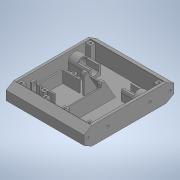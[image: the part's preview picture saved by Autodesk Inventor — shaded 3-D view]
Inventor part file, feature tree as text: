
AUTODESK INVENTOR PART (.ipt)
format: ipt  version: 2020 (Build 240168000, 168)  size: 648,192 bytes
history: native  units: in
note: dims shown in document units (in); Inventor stores cm internally (conversion verified against a paired STEP export)
features: extrude x19, sketch x19, projected_geometry x14, mirror x6, plane x1
ambient origin geometry x8: Origin, YZ Plane, XZ Plane, XY Plane, X Axis, Y Axis, Z Axis, Center Point
bodies: Solid1 (feature_tree)
feature tree (59):
  extrude  "Extrusion1"  Depth=5.9055in
  extrude  "Extrusion2"  TaperAngle=0.0deg  [1 undecoded]
  extrude  "Extrusion3"  Depth=1.063in
  extrude  "Extrusion4"  Depth=0.315in
  extrude  "Extrusion5"  TaperAngle=0.0deg  [1 undecoded]
  extrude  "Extrusion6"  Depth=0.5906in
  mirror  "Mirror1"
  extrude  "Extrusion7"  Depth=0.0787in
  mirror  "Mirror2"
  extrude  "Extrusion8"  Depth=0.6102in
  mirror  "Mirror3"
  plane  "Work Plane1"
  extrude  "Extrusion9"  Depth=0.7874in TaperAngle=0.0deg
  mirror  "Mirror4"
  extrude  "Extrusion10"  Depth=6.063in TaperAngle=0.0deg
  extrude  "Extrusion11"  Depth=0.1575in
  extrude  "Extrusion12"  TaperAngle=0.0deg  [1 undecoded]
  extrude  "Extrusion13"  Depth=0.2756in
  extrude  "Extrusion14"  Depth=0.4331in
  extrude  "Extrusion17"  Depth=2.7559in
  extrude  "Extrusion18"  Depth=0.0453in
  mirror  "Mirror6"
  extrude  "Extrusion19"  TaperAngle=0.0deg  [1 undecoded]
  mirror  "Mirror7"
  extrude  "Extrusion20"  Depth=0.0787in
  extrude  "Extrusion21"  Depth=0.993in
  sketch  "Sketch1"  dims[d0=1.1811in d1=5.9055in]
  sketch  "Sketch2"  dims[d2=5.1181in d3=0.0in]
  projected_geometry  "Projected Loop1"
  sketch  "Sketch3"  dims[d4=0.1575in d5=1.063in]
  projected_geometry  "Projected Loop2"
  projected_geometry  "Projected Loop3"
  sketch  "Sketch4"  dims[d6=0.0in d8=0.315in]
  sketch  "Sketch5"  dims[d10=0.993in d11=0.0in]
  projected_geometry  "Projected Loop4"
  sketch  "Sketch6"  dims[d12=0.6496in d13=0.5906in]
  sketch  "Sketch7"  dims[d14=1.5748in d15=0.0787in]
  sketch  "Sketch9"  dims[d16=0.5512in d17=0.0in d18=0.6102in]
  sketch  "Sketch10"  dims[d19=0.4803in d20=0.7874in d21=0.0in]
  sketch  "Sketch12"  dims[d22=0.1654in d23=6.063in d24=0.0in]
  projected_geometry  "Projected Loop6"
  projected_geometry  "Projected Loop7"
  projected_geometry  "Projected Loop8"
  sketch  "Sketch13"  dims[d25=0.5114in d26=0.1575in]
  sketch  "Sketch14"  dims[d27=1.5748in d28=0.0in d29=0.0in]
  sketch  "Sketch15"  dims[d30=0.1575in d31=0.2756in]
  projected_geometry  "Projected Loop15"
  sketch  "Sketch16"  dims[d32=0.0in d33=0.4331in]
  projected_geometry  "Projected Loop19"
  projected_geometry  "Projected Loop20"
  projected_geometry  "Projected Loop21"
  projected_geometry  "Projected Loop22"
  projected_geometry  "Projected Loop23"
  projected_geometry  "Projected Loop24"
  sketch  "Sketch20"  dims[d34=0.0906in d38=2.7559in]
  sketch  "Sketch21"  dims[d40=0.0453in d41=0.0909in]
  sketch  "Sketch22"  dims[d42=0.2362in d43=0.0in]
  sketch  "Sketch23"  dims[d44=60.0deg d45=0.0787in]
  sketch  "Sketch25"  dims[d46=0.315in d48=0.993in d49=0.0in d53=0.2756in d54=0.0in d55=0.4724in d56=1.1811in d57=1.5748in d58=1.5748in d59=0.0787in d60=0.0787in d62=0.315in d63=0.7677in d64=0.0in d66=0.1476in d67=0.2756in d68=0.0in d69=0.7874in d70=0.2953in d71=0.1181in d72=0.0in d89=0.0157in d90=0.0157in d91=0.1476in d92=0.1476in d96=0.315in d97=0.1575in d98=0.1181in d99=0.0in d102=0.1772in d104=0.3346in d105=135.0deg d106=0.2362in d107=0.0in d108=0.0394in d109=0.0in d110=0.063in d111=0.0394in d112=0.0in d117=0.993in d118=0.063in d119=0.3937in d120=0.0in]
note: 4 required parameter values undecoded (feature->parameter linkage not recoverable at this tier; creation-order binding heuristic only, values carry confidence <= 0.55)
